# Revit family: HansWeitzel_2282
name_source: partatom
category: Allgemeines Modell
revit_build: Autodesk Revit 2017 (Build: 20160225_1515(x64)
units: mm (PartAtom-declared; Revit-internal decimal feet)

## family parameters
Basisbauteil = Wand
Beim Laden mit Abzugskörper schneiden = Nein
Bemaßung runder Anschluss = Durchmesser verwenden
Gemeinsam genutzt = Nein
Immer vertikal = Ja
Kann Basisbauteil für Bewehrung sein = Nein
Raumberechnungspunkt = Nein
Teiletyp = Normal

## types (1)
- Type 1
    BIM = https://media.live.bim.site
    BIMSITE_PRODUCT_ID = 5dcb47081f2577f40a5d392030c4f308c767ae65
    Beschreibung = HZ-Außenecke SLT Weiß für HZ-Sockelleiste SLT nur mit SCH2152
    Breite [mm] = 70
    Dekor = Weiß
    Farbton = weiß
    GTIN = 4022023212617
    Gewicht unverpackt (netto) [kg] = 0.002
    HAN = 2282
    HeinzeBIM = https://www.heinze.de
    Hersteller = Hans Weitzel GmbH & Co. KG
    Höhe [mm] = 89
    Ist System = Nein
    Ist Zubehör = Nein
    Length3 = 100 mm  [stored 0.328084 ft]
    Menge pro Verpackungseinheit = 10
    Profilart = Außeneckprofil
    Profilform = Eckprofil
    Tiefe (mm) = 81
    Typname = HZ-Außenecke SLT Weiß
    Werkstoff = Polystyrol
    max. Betriebstemperatur (°C) = 90

note: [stored X ft] marks values corroborated as IEEE doubles in the binary element streams (Revit-internal decimal feet)

## geometry (parser evidence)
native form markers: Sweep x5
no freeform markers — native parametric forms only
